# Revit family: 02-60-0035 DN40-500
name_source: partatom
category: Plumbing Fixtures
units: mm (PartAtom-declared; Revit-internal decimal feet)

## family parameters
Always vertical = Yes
Cut with Voids When Loaded = No
Maintain Annotation Orientation = No
Part Type = Normal
Room Calculation Point = No
Round Connector Dimension = Use Diameter
Shared = No
Work Plane-Based = No

## types (21) — shared parameters
1 = 1 mm  [stored 0.00328084 ft]
5 = 5 mm  [stored 0.0164042 ft]
DN040_PN10/16 = 02-040-60-014649
DN050_PN10/16 = 02-050-60-014649
DN065_PN10/16 = 02-065-60-014649
DN080_PN10/16 = 02-080-60-014649
DN100_PN10/16 = 02-100-60-014649
DN125_PN10/16 = 02-125-60-014649
DN150_PN10/16 = 02-150-60-014649
DN200_PN10 = 02-200-60-004649
DN200_PN16 = 02-200-60-014649
DN250_PN10 = 02-250-60-004649
DN250_PN16 = 02-250-60-014649
DN300_PN10 = 02-300-60-004647
DN300_PN16 = 02-300-60-014647
DN350_PN10 = 02-350-60-006
DN350_PN16 = 02-350-60-016
DN400_PN10 = 02-400-60-006
DN400_PN16 = 02-400-60-016
DN450_PN10 = 02-450-60-006
DN450_PN16 = 02-450-60-016
DN500_PN10 = 02-500-60-006
DN500_PN16 = 02-500-60-016
Description_ = AVK GATE VALVE, FLANGED, PN10-16
Search_table = 02-60-0035 DN40-500
URL_product_pages = https://www.avkvalves.com
zero-valued in all types: 50, Default Elevation, Rib4_H, Rib4_L, Rib4_W, Rib5_H, Rib5_L, Rib5_W

## per-type parameters (varying)
- DN040_PN10/16: Body_Arc=125 mm; Body_FL_L=60 mm; Body_FL_R=18 mm  [stored 0.0590551 ft]; Body_FL_T=9 mm  [stored 0.0295276 ft]; Body_FL_W=50 mm; Body_FL_arc=150 mm; Body_FL_rib_dim=164 mm; Body_FL_rib_dim1=105 mm; Body_H=95 mm; Body_L=45 mm; Body_R=8 mm  [stored 0.0262467 ft]; Body_T=10 mm  [stored 0.0328084 ft]; Body_W=43 mm; Body_bottom=15 mm  [stored 0.0492126 ft]; Bonnet_L=41 mm; Bonnet_d1=35 mm  [stored 0.114829 ft]; Bonnet_d2=22 mm  [stored 0.0721785 ft]; Bonnet_dim1=38 mm  [stored 0.124672 ft]; Bonnet_dim2=35 mm  [stored 0.114829 ft]; Bonnet_dim3=23 mm  [stored 0.0754593 ft]; Bore_R=20 mm  [stored 0.0656168 ft]; DN=40 mm; Dh=110 mm; Ds=19 mm  [stored 0.062336 ft]; F=7 mm  [stored 0.0229659 ft]; F1=9 mm  [stored 0.0295276 ft]; F2=29 mm  [stored 0.0951444 ft]; FL_R=70 mm; FL_T=15 mm  [stored 0.0492126 ft]; H=194 mm; H3=269 mm; H3-H=75 mm; L=240 mm; RIB_L=74 mm; RIB_L1=49 mm; RIB_T=6 mm  [stored 0.019685 ft]; Raised_R=45 mm; Raised_dis=3 mm  [stored 0.00984252 ft]; Rib1_H=50 mm; Rib1_L=75 mm; Rib1_R=18 mm  [stored 0.0590551 ft]; Rib1_T=4 mm  [stored 0.0131234 ft]; Rib1_W=45 mm; Rib2_H=50 mm; Rib2_L=70 mm; Rib2_W=45 mm; Rib3_H=50 mm; Rib3_L=50 mm; Rib3_W=45 mm; Rib_T=12 mm  [stored 0.0393701 ft]; Stem=12 mm  [stored 0.0393701 ft]; Sweep _cut=2 mm  [stored 0.00656168 ft]; W=75 mm; Wedge_L=37 mm; logo_H=48 mm; stem1=12 mm  [stored 0.0393701 ft]
- DN050_PN10/16: Body_Arc=150 mm; Body_FL_L=67 mm; Body_FL_R=20 mm  [stored 0.0656168 ft]; Body_FL_T=10 mm  [stored 0.0328084 ft]; Body_FL_W=52 mm; Body_FL_arc=200 mm; Body_FL_rib_dim=179 mm; Body_FL_rib_dim1=106 mm; Body_H=110 mm; Body_L=52 mm; Body_R=10 mm  [stored 0.0328084 ft]; Body_T=10 mm  [stored 0.0328084 ft]; Body_W=45 mm; Body_bottom=22 mm  [stored 0.0721785 ft]; Bonnet_L=47 mm; Bonnet_d1=36 mm  [stored 0.11811 ft]; Bonnet_d2=23 mm  [stored 0.0754593 ft]; Bonnet_dim1=38 mm  [stored 0.124672 ft]; Bonnet_dim2=36 mm  [stored 0.11811 ft]; Bonnet_dim3=23 mm  [stored 0.0754593 ft]; Bore_R=25 mm  [stored 0.082021 ft]; DN=50 mm; Dh=125 mm; Ds=19 mm  [stored 0.062336 ft]; F=7 mm  [stored 0.0229659 ft]; F1=9 mm  [stored 0.0295276 ft]; F2=29 mm  [stored 0.0951444 ft]; FL_R=83 mm; FL_T=19 mm  [stored 0.062336 ft]; H=209 mm; H3=292 mm; H3-H=83 mm; L=250 mm; RIB_L=82 mm; RIB_L1=54 mm; RIB_T=6 mm  [stored 0.019685 ft]; Raised_R=49 mm; Raised_dis=3 mm  [stored 0.00984252 ft]; Rib1_H=60 mm; Rib1_L=80 mm; Rib1_R=20 mm  [stored 0.0656168 ft]; Rib1_T=5 mm  [stored 0.0164042 ft]; Rib1_W=50 mm; Rib2_H=60 mm; Rib2_L=80 mm; Rib2_W=50 mm; Rib3_H=60 mm; Rib3_L=80 mm; Rib3_W=50 mm; Rib_T=16 mm  [stored 0.0524934 ft]; Stem=12 mm  [stored 0.0393701 ft]; Sweep _cut=2 mm  [stored 0.00656168 ft]; W=83 mm; Wedge_L=38 mm  [stored 0.124672 ft]; logo_H=55 mm; stem1=12 mm  [stored 0.0393701 ft]
- DN065_PN10/16: Body_Arc=206 mm; Body_FL_L=86 mm; Body_FL_R=20 mm  [stored 0.0656168 ft]; Body_FL_T=11 mm  [stored 0.0360892 ft]; Body_FL_W=56 mm; Body_FL_arc=775 mm; Body_FL_rib_dim=213 mm; Body_FL_rib_dim1=116 mm; Body_H=102 mm; Body_L=74 mm; Body_R=15 mm  [stored 0.0492126 ft]; Body_T=7 mm  [stored 0.0229659 ft]; Body_W=49 mm; Body_bottom=44 mm; Bonnet_L=67 mm; Bonnet_d1=39 mm; Bonnet_d2=24 mm  [stored 0.0787402 ft]; Bonnet_dim1=48 mm; Bonnet_dim2=39 mm; Bonnet_dim3=29 mm  [stored 0.0951444 ft]; Bore_R=33 mm; DN=65 mm; Dh=154 mm; Ds=19 mm  [stored 0.062336 ft]; F=9 mm  [stored 0.0295276 ft]; F1=12 mm  [stored 0.0393701 ft]; F2=34 mm  [stored 0.111549 ft]; FL_R=97 mm; FL_T=19 mm  [stored 0.062336 ft]; H=243 mm; H3=336 mm; H3-H=93 mm; L=270 mm; RIB_L=94 mm; RIB_L1=62 mm; RIB_T=6 mm  [stored 0.019685 ft]; Raised_R=64 mm; Raised_dis=3 mm  [stored 0.00984252 ft]; Rib1_H=50 mm; Rib1_L=120 mm; Rib1_R=20 mm  [stored 0.0656168 ft]; Rib1_T=5 mm  [stored 0.0164042 ft]; Rib1_W=60 mm; Rib2_H=50 mm; Rib2_L=120 mm; Rib2_W=60 mm; Rib3_H=50 mm; Rib3_L=120 mm; Rib3_W=60 mm; Rib_T=16 mm  [stored 0.0524934 ft]; Stem=14 mm  [stored 0.0459318 ft]; Sweep _cut=2 mm  [stored 0.00656168 ft]; W=95 mm; Wedge_L=41 mm; logo_H=51 mm; stem1=16 mm  [stored 0.0524934 ft]
- DN080_PN10/16: Body_Arc=212 mm; Body_FL_L=86 mm; Body_FL_R=20 mm  [stored 0.0656168 ft]; Body_FL_T=12 mm  [stored 0.0393701 ft]; Body_FL_W=58 mm; Body_FL_arc=775 mm; Body_FL_rib_dim=252 mm; Body_FL_rib_dim1=121 mm; Body_H=108 mm; Body_L=72 mm; Body_R=16 mm  [stored 0.0524934 ft]; Body_T=7 mm  [stored 0.0229659 ft]; Body_W=50 mm; Body_bottom=42 mm; Bonnet_L=65 mm; Bonnet_d1=40 mm; Bonnet_d2=25 mm  [stored 0.082021 ft]; Bonnet_dim1=48 mm; Bonnet_dim2=41 mm; Bonnet_dim3=29 mm  [stored 0.0951444 ft]; Bore_R=40 mm; DN=80 mm; Dh=160 mm; Ds=19 mm  [stored 0.062336 ft]; F=9 mm  [stored 0.0295276 ft]; F1=12 mm  [stored 0.0393701 ft]; F2=34 mm  [stored 0.111549 ft]; FL_R=100 mm; FL_T=19 mm  [stored 0.062336 ft]; H=282 mm; H3=382 mm; H3-H=100 mm; L=280 mm; RIB_L=99 mm; RIB_L1=65 mm; RIB_T=6 mm  [stored 0.019685 ft]; Raised_R=66 mm; Raised_dis=3 mm  [stored 0.00984252 ft]; Rib1_H=58 mm; Rib1_L=120 mm; Rib1_R=20 mm  [stored 0.0656168 ft]; Rib1_T=5 mm  [stored 0.0164042 ft]; Rib1_W=60 mm; Rib2_H=58 mm; Rib2_L=120 mm; Rib2_W=60 mm; Rib3_H=58 mm; Rib3_L=120 mm; Rib3_W=60 mm; Rib_T=16 mm  [stored 0.0524934 ft]; Stem=14 mm  [stored 0.0459318 ft]; Sweep _cut=2 mm  [stored 0.00656168 ft]; W=100 mm; Wedge_L=43 mm; logo_H=54 mm; stem1=16 mm  [stored 0.0524934 ft]
- DN100_PN10/16: Body_Arc=220 mm; Body_FL_L=96 mm; Body_FL_R=20 mm  [stored 0.0656168 ft]; Body_FL_T=13 mm; Body_FL_W=62 mm; Body_FL_arc=400 mm; Body_FL_rib_dim=276 mm; Body_FL_rib_dim1=132 mm; Body_H=122 mm; Body_L=82 mm; Body_R=16 mm  [stored 0.0524934 ft]; Body_T=6 mm  [stored 0.019685 ft]; Body_W=54 mm; Body_bottom=52 mm; Bonnet_L=74 mm; Bonnet_d1=43 mm; Bonnet_d2=27 mm  [stored 0.0885827 ft]; Bonnet_dim1=48 mm; Bonnet_dim2=43 mm; Bonnet_dim3=29 mm  [stored 0.0951444 ft]; Bore_R=50 mm; DN=100 mm; Dh=180 mm; Ds=19 mm  [stored 0.062336 ft]; F=10 mm  [stored 0.0328084 ft]; F1=12 mm  [stored 0.0393701 ft]; F2=34 mm  [stored 0.111549 ft]; FL_R=110 mm; FL_T=18 mm  [stored 0.0590551 ft]; H=306 mm; H3=416 mm; H3-H=110 mm; L=300 mm; RIB_L=117 mm; RIB_L1=76 mm; RIB_T=6 mm  [stored 0.019685 ft]; Raised_R=77 mm; Raised_dis=3 mm  [stored 0.00984252 ft]; Rib1_H=72 mm; Rib1_L=120 mm; Rib1_R=20 mm  [stored 0.0656168 ft]; Rib1_T=5 mm  [stored 0.0164042 ft]; Rib1_W=60 mm; Rib2_H=72 mm; Rib2_L=120 mm; Rib2_W=60 mm; Rib3_H=72 mm; Rib3_L=120 mm; Rib3_W=60 mm; Rib_T=15 mm  [stored 0.0492126 ft]; Stem=14 mm  [stored 0.0459318 ft]; Sweep _cut=2 mm  [stored 0.00656168 ft]; W=118 mm; Wedge_L=46 mm; logo_H=61 mm; stem1=16 mm  [stored 0.0524934 ft]
- DN125_PN10/16: Body_Arc=300 mm; Body_FL_L=110 mm; Body_FL_R=20 mm  [stored 0.0656168 ft]; Body_FL_T=13 mm; Body_FL_W=67 mm; Body_FL_arc=450 mm; Body_FL_rib_dim=316 mm; Body_FL_rib_dim1=145 mm; Body_H=145 mm; Body_L=100 mm; Body_R=16 mm  [stored 0.0524934 ft]; Body_T=6 mm  [stored 0.019685 ft]; Body_W=59 mm; Body_bottom=70 mm; Bonnet_L=90 mm; Bonnet_d1=47 mm; Bonnet_d2=29 mm  [stored 0.0951444 ft]; Bonnet_dim1=48 mm; Bonnet_dim2=47 mm; Bonnet_dim3=29 mm  [stored 0.0951444 ft]; Bore_R=63 mm; DN=125 mm; Dh=190 mm; Ds=20 mm  [stored 0.0656168 ft]; F=10 mm  [stored 0.0328084 ft]; F1=12 mm  [stored 0.0393701 ft]; F2=34 mm  [stored 0.111549 ft]; FL_R=135 mm; FL_T=18 mm  [stored 0.0590551 ft]; H=346 mm; H3=471 mm; H3-H=125 mm; L=325 mm; RIB_L=134 mm; RIB_L1=88 mm; RIB_T=6 mm  [stored 0.019685 ft]; Raised_R=80 mm; Raised_dis=3 mm  [stored 0.00984252 ft]; Rib1_H=90 mm; Rib1_L=120 mm; Rib1_R=20 mm  [stored 0.0656168 ft]; Rib1_T=5 mm  [stored 0.0164042 ft]; Rib1_W=60 mm; Rib2_H=90 mm; Rib2_L=120 mm; Rib2_W=60 mm; Rib3_H=100 mm; Rib3_L=120 mm; Rib3_W=60 mm; Rib_T=15 mm  [stored 0.0492126 ft]; Stem=14 mm  [stored 0.0459318 ft]; Sweep _cut=2 mm  [stored 0.00656168 ft]; W=135 mm; Wedge_L=50 mm; logo_H=73 mm; stem1=16 mm  [stored 0.0524934 ft]
- DN150_PN10/16: Body_Arc=400 mm; Body_FL_L=136 mm; Body_FL_R=20 mm  [stored 0.0656168 ft]; Body_FL_T=13 mm; Body_FL_W=72 mm; Body_FL_arc=300 mm; Body_FL_rib_dim=373 mm; Body_FL_rib_dim1=157 mm; Body_H=172 mm; Body_L=122 mm; Body_R=16 mm  [stored 0.0524934 ft]; Body_T=6 mm  [stored 0.019685 ft]; Body_W=63 mm; Body_bottom=92 mm; Bonnet_L=110 mm; Bonnet_d1=50 mm; Bonnet_d2=32 mm  [stored 0.104987 ft]; Bonnet_dim1=46 mm; Bonnet_dim2=51 mm; Bonnet_dim3=28 mm  [stored 0.0918635 ft]; Bore_R=75 mm; DN=150 mm; Dh=240 mm; Ds=23 mm  [stored 0.0754593 ft]; F=10 mm  [stored 0.0328084 ft]; F1=11 mm  [stored 0.0360892 ft]; F2=34 mm  [stored 0.111549 ft]; FL_R=143 mm; FL_T=18 mm  [stored 0.0590551 ft]; H=403 mm; H3=543 mm; H3-H=140 mm; L=350 mm; RIB_L=149 mm; RIB_L1=98 mm; RIB_T=6 mm  [stored 0.019685 ft]; Raised_R=106 mm; Raised_dis=3 mm  [stored 0.00984252 ft]; Rib1_H=122 mm; Rib1_L=120 mm; Rib1_R=20 mm  [stored 0.0656168 ft]; Rib1_T=5 mm  [stored 0.0164042 ft]; Rib1_W=60 mm; Rib2_H=122 mm; Rib2_L=120 mm; Rib2_W=60 mm; Rib3_H=122 mm; Rib3_L=120 mm; Rib3_W=60 mm; Rib_T=15 mm  [stored 0.0492126 ft]; Stem=14 mm  [stored 0.0459318 ft]; Sweep _cut=2 mm  [stored 0.00656168 ft]; W=150 mm; Wedge_L=54 mm; logo_H=86 mm; stem1=15 mm  [stored 0.0492126 ft]
- DN200_PN10: Body_Arc=500 mm; Body_FL_L=166 mm; Body_FL_R=25 mm  [stored 0.082021 ft]; Body_FL_T=15 mm  [stored 0.0492126 ft]; Body_FL_W=83 mm; Body_FL_arc=450 mm; Body_FL_rib_dim=460 mm; Body_FL_rib_dim1=180 mm; Body_H=220 mm; Body_L=157 mm; Body_R=20 mm  [stored 0.0656168 ft]; Body_T=7 mm  [stored 0.0229659 ft]; Body_W=72 mm; Body_bottom=127 mm; Bonnet_L=141 mm; Bonnet_d1=58 mm; Bonnet_d2=36 mm  [stored 0.11811 ft]; Bonnet_dim1=59 mm; Bonnet_dim2=58 mm; Bonnet_dim3=35 mm  [stored 0.114829 ft]; Bore_R=100 mm; DN=200 mm; Dh=295 mm; Ds=23 mm  [stored 0.0754593 ft]; F=12 mm  [stored 0.0393701 ft]; F1=14 mm  [stored 0.0459318 ft]; F2=34 mm  [stored 0.111549 ft]; FL_R=170 mm; FL_T=20 mm  [stored 0.0656168 ft]; H=490 mm; H3=660 mm; H3-H=170 mm; L=400 mm; RIB_L=187 mm; RIB_L1=122 mm; RIB_T=6 mm  [stored 0.019685 ft]; Raised_R=132 mm; Raised_dis=3 mm  [stored 0.00984252 ft]; Rib1_H=170 mm; Rib1_L=120 mm; Rib1_R=20 mm  [stored 0.0656168 ft]; Rib1_T=5 mm  [stored 0.0164042 ft]; Rib1_W=60 mm; Rib2_H=170 mm; Rib2_L=120 mm; Rib2_W=60 mm; Rib3_H=170 mm; Rib3_L=120 mm; Rib3_W=60 mm; Rib_T=17 mm  [stored 0.0557743 ft]; Stem=14 mm  [stored 0.0459318 ft]; Sweep _cut=3 mm  [stored 0.00984252 ft]; W=188 mm; Wedge_L=61 mm; logo_H=110 mm; stem1=19 mm  [stored 0.062336 ft]
- DN200_PN16: Body_Arc=500 mm; Body_FL_L=166 mm; Body_FL_R=25 mm  [stored 0.082021 ft]; Body_FL_T=15 mm  [stored 0.0492126 ft]; Body_FL_W=83 mm; Body_FL_arc=450 mm; Body_FL_rib_dim=460 mm; Body_FL_rib_dim1=180 mm; Body_H=220 mm; Body_L=157 mm; Body_R=20 mm  [stored 0.0656168 ft]; Body_T=7 mm  [stored 0.0229659 ft]; Body_W=72 mm; Body_bottom=127 mm; Bonnet_L=141 mm; Bonnet_d1=58 mm; Bonnet_d2=36 mm  [stored 0.11811 ft]; Bonnet_dim1=59 mm; Bonnet_dim2=58 mm; Bonnet_dim3=35 mm  [stored 0.114829 ft]; Bore_R=100 mm; DN=200 mm; Dh=295 mm; Ds=23 mm  [stored 0.0754593 ft]; F=12 mm  [stored 0.0393701 ft]; F1=14 mm  [stored 0.0459318 ft]; F2=34 mm  [stored 0.111549 ft]; FL_R=170 mm; FL_T=20 mm  [stored 0.0656168 ft]; H=490 mm; H3=660 mm; H3-H=170 mm; L=400 mm; RIB_L=187 mm; RIB_L1=122 mm; RIB_T=6 mm  [stored 0.019685 ft]; Raised_R=132 mm; Raised_dis=3 mm  [stored 0.00984252 ft]; Rib1_H=170 mm; Rib1_L=120 mm; Rib1_R=20 mm  [stored 0.0656168 ft]; Rib1_T=5 mm  [stored 0.0164042 ft]; Rib1_W=60 mm; Rib2_H=170 mm; Rib2_L=120 mm; Rib2_W=60 mm; Rib3_H=170 mm; Rib3_L=120 mm; Rib3_W=60 mm; Rib_T=17 mm  [stored 0.0557743 ft]; Stem=14 mm  [stored 0.0459318 ft]; Sweep _cut=3 mm  [stored 0.00984252 ft]; W=188 mm; Wedge_L=61 mm; logo_H=110 mm; stem1=19 mm  [stored 0.062336 ft]
- DN300_PN10: Body_Arc=900 mm; Body_FL_L=228 mm; Body_FL_R=30 mm  [stored 0.0984252 ft]; Body_FL_T=23 mm  [stored 0.0754593 ft]; Body_FL_W=104 mm; Body_FL_arc=1000 mm; Body_FL_rib_dim=676 mm; Body_FL_rib_dim1=230 mm; Body_H=370 mm; Body_L=205 mm; Body_R=30 mm  [stored 0.0984252 ft]; Body_T=9 mm  [stored 0.0295276 ft]; Body_W=90 mm; Body_bottom=175 mm; Bonnet_L=185 mm; Bonnet_d1=72 mm; Bonnet_d2=45 mm; Bonnet_dim1=76 mm; Bonnet_dim2=72 mm; Bonnet_dim3=45 mm; Bore_R=150 mm; DN=300 mm; Dh=400 mm; Ds=23 mm  [stored 0.0754593 ft]; F=14 mm  [stored 0.0459318 ft]; F1=18 mm  [stored 0.0590551 ft]; F2=47 mm; FL_R=228 mm; FL_T=20 mm  [stored 0.0656168 ft]; H=706 mm; H3=934 mm; H3-H=228 mm; L=500 mm; RIB_L=227 mm; RIB_L1=148 mm; RIB_T=4 mm  [stored 0.0131234 ft]; Raised_R=184 mm; Raised_dis=2 mm  [stored 0.00656168 ft]; Rib1_H=245 mm; Rib1_L=432 mm; Rib1_R=65 mm; Rib1_T=8 mm  [stored 0.0262467 ft]; Rib1_W=220 mm; Rib2_H=170 mm; Rib2_L=432 mm; Rib2_W=220 mm; Rib3_H=190 mm; Rib3_L=280 mm; Rib3_W=150 mm; Rib_T=18 mm  [stored 0.0590551 ft]; Stem=19 mm  [stored 0.062336 ft]; Sweep _cut=4 mm  [stored 0.0131234 ft]; W=228 mm; Wedge_L=77 mm; logo_H=185 mm; stem1=24 mm  [stored 0.0787402 ft]
- DN300_PN16: Body_Arc=900 mm; Body_FL_L=228 mm; Body_FL_R=30 mm  [stored 0.0984252 ft]; Body_FL_T=23 mm  [stored 0.0754593 ft]; Body_FL_W=104 mm; Body_FL_arc=1000 mm; Body_FL_rib_dim=676 mm; Body_FL_rib_dim1=230 mm; Body_H=370 mm; Body_L=205 mm; Body_R=30 mm  [stored 0.0984252 ft]; Body_T=9 mm  [stored 0.0295276 ft]; Body_W=90 mm; Body_bottom=175 mm; Bonnet_L=185 mm; Bonnet_d1=72 mm; Bonnet_d2=45 mm; Bonnet_dim1=76 mm; Bonnet_dim2=72 mm; Bonnet_dim3=45 mm; Bore_R=150 mm; DN=300 mm; Dh=410 mm; Ds=28 mm  [stored 0.0918635 ft]; F=14 mm  [stored 0.0459318 ft]; F1=18 mm  [stored 0.0590551 ft]; F2=47 mm; FL_R=228 mm; FL_T=20 mm  [stored 0.0656168 ft]; H=706 mm; H3=934 mm; H3-H=228 mm; L=500 mm; RIB_L=227 mm; RIB_L1=148 mm; RIB_T=4 mm  [stored 0.0131234 ft]; Raised_R=184 mm; Raised_dis=2 mm  [stored 0.00656168 ft]; Rib1_H=245 mm; Rib1_L=432 mm; Rib1_R=65 mm; Rib1_T=8 mm  [stored 0.0262467 ft]; Rib1_W=220 mm; Rib2_H=170 mm; Rib2_L=432 mm; Rib2_W=220 mm; Rib3_H=190 mm; Rib3_L=280 mm; Rib3_W=150 mm; Rib_T=18 mm  [stored 0.0590551 ft]; Stem=19 mm  [stored 0.062336 ft]; Sweep _cut=4 mm  [stored 0.0131234 ft]; W=228 mm; Wedge_L=77 mm; logo_H=185 mm; stem1=24 mm  [stored 0.0787402 ft]
- DN350_PN10: Body_Arc=1120 mm; Body_FL_L=282 mm; Body_FL_R=40 mm; Body_FL_T=28 mm  [stored 0.0918635 ft]; Body_FL_W=114 mm; Body_FL_arc=1550 mm; Body_FL_rib_dim=917 mm; Body_FL_rib_dim1=251 mm; Body_H=485 mm; Body_L=238 mm; Body_R=30 mm  [stored 0.0984252 ft]; Body_T=13 mm; Body_W=99 mm; Body_bottom=208 mm; Bonnet_L=214 mm; Bonnet_d1=79 mm; Bonnet_d2=50 mm; Bonnet_dim1=84 mm; Bonnet_dim2=80 mm; Bonnet_dim3=50 mm; Bore_R=175 mm; DN=350 mm; Dh=460 mm; Ds=23 mm  [stored 0.0754593 ft]; F=16 mm  [stored 0.0524934 ft]; F1=20 mm  [stored 0.0656168 ft]; F2=55 mm; FL_R=520 mm; FL_T=25 mm  [stored 0.082021 ft]; H=947 mm; H3=1207 mm; H3-H=260 mm; L=550 mm; RIB_L=281 mm; RIB_L1=183 mm; RIB_T=8 mm  [stored 0.0262467 ft]; Raised_R=215 mm; Raised_dis=4 mm  [stored 0.0131234 ft]; Rib1_H=410 mm; Rib1_L=560 mm; Rib1_R=65 mm; Rib1_T=9 mm  [stored 0.0295276 ft]; Rib1_W=306 mm; Rib2_H=290 mm; Rib2_L=560 mm; Rib2_W=306 mm; Rib3_H=170 mm; Rib3_L=560 mm; Rib3_W=306 mm; Rib_T=21 mm; Stem=22 mm  [stored 0.0721785 ft]; Sweep _cut=5 mm  [stored 0.0164042 ft]; W=282 mm; Wedge_L=84 mm; logo_H=243 mm; stem1=27 mm  [stored 0.0885827 ft]
- DN350_PN16: Body_Arc=1120 mm; Body_FL_L=282 mm; Body_FL_R=40 mm; Body_FL_T=28 mm  [stored 0.0918635 ft]; Body_FL_W=114 mm; Body_FL_arc=1550 mm; Body_FL_rib_dim=917 mm; Body_FL_rib_dim1=251 mm; Body_H=485 mm; Body_L=238 mm; Body_R=30 mm  [stored 0.0984252 ft]; Body_T=13 mm; Body_W=99 mm; Body_bottom=208 mm; Bonnet_L=214 mm; Bonnet_d1=79 mm; Bonnet_d2=50 mm; Bonnet_dim1=84 mm; Bonnet_dim2=80 mm; Bonnet_dim3=50 mm; Bore_R=175 mm; DN=350 mm; Dh=470 mm; Ds=28 mm  [stored 0.0918635 ft]; F=16 mm  [stored 0.0524934 ft]; F1=20 mm  [stored 0.0656168 ft]; F2=55 mm; FL_R=520 mm; FL_T=25 mm  [stored 0.082021 ft]; H=947 mm; H3=1207 mm; H3-H=260 mm; L=550 mm; RIB_L=281 mm; RIB_L1=183 mm; RIB_T=8 mm  [stored 0.0262467 ft]; Raised_R=215 mm; Raised_dis=4 mm  [stored 0.0131234 ft]; Rib1_H=410 mm; Rib1_L=560 mm; Rib1_R=65 mm; Rib1_T=9 mm  [stored 0.0295276 ft]; Rib1_W=306 mm; Rib2_H=290 mm; Rib2_L=560 mm; Rib2_W=306 mm; Rib3_H=170 mm; Rib3_L=560 mm; Rib3_W=306 mm; Rib_T=21 mm; Stem=22 mm  [stored 0.0721785 ft]; Sweep _cut=5 mm  [stored 0.0164042 ft]; W=282 mm; Wedge_L=84 mm; logo_H=243 mm; stem1=27 mm  [stored 0.0885827 ft]
- DN400_PN10: Body_Arc=1120 mm; Body_FL_L=290 mm; Body_FL_R=50 mm; Body_FL_T=30 mm  [stored 0.0984252 ft]; Body_FL_W=124 mm; Body_FL_arc=1159 mm; Body_FL_rib_dim=929 mm; Body_FL_rib_dim1=276 mm; Body_H=512 mm; Body_L=238 mm; Body_R=30 mm  [stored 0.0984252 ft]; Body_T=13 mm; Body_W=108 mm; Body_bottom=208 mm; Bonnet_L=214 mm; Bonnet_d1=86 mm; Bonnet_d2=54 mm; Bonnet_dim1=84 mm; Bonnet_dim2=87 mm; Bonnet_dim3=50 mm; Bore_R=200 mm; DN=400 mm; Dh=515 mm; Ds=28 mm  [stored 0.0918635 ft]; F=16 mm  [stored 0.0524934 ft]; F1=20 mm  [stored 0.0656168 ft]; F2=55 mm; FL_R=290 mm; FL_T=25 mm  [stored 0.082021 ft]; H=959 mm; H3=1249 mm; H3-H=290 mm; L=600 mm; RIB_L=289 mm; RIB_L1=189 mm; RIB_T=8 mm  [stored 0.0262467 ft]; Raised_R=241 mm; Raised_dis=4 mm  [stored 0.0131234 ft]; Rib1_H=430 mm; Rib1_L=538 mm; Rib1_R=70 mm; Rib1_T=10 mm  [stored 0.0328084 ft]; Rib1_W=326 mm; Rib2_H=320 mm; Rib2_L=538 mm; Rib2_W=326 mm; Rib3_H=173 mm; Rib3_L=538 mm; Rib3_W=326 mm; Rib_T=21 mm; Stem=22 mm  [stored 0.0721785 ft]; Sweep _cut=5 mm  [stored 0.0164042 ft]; W=290 mm; Wedge_L=92 mm; logo_H=256 mm; stem1=27 mm  [stored 0.0885827 ft]
- DN400_PN16: Body_Arc=1120 mm; Body_FL_L=290 mm; Body_FL_R=50 mm; Body_FL_T=30 mm  [stored 0.0984252 ft]; Body_FL_W=124 mm; Body_FL_arc=1159 mm; Body_FL_rib_dim=929 mm; Body_FL_rib_dim1=276 mm; Body_H=512 mm; Body_L=238 mm; Body_R=30 mm  [stored 0.0984252 ft]; Body_T=13 mm; Body_W=108 mm; Body_bottom=208 mm; Bonnet_L=214 mm; Bonnet_d1=86 mm; Bonnet_d2=54 mm; Bonnet_dim1=84 mm; Bonnet_dim2=87 mm; Bonnet_dim3=50 mm; Bore_R=200 mm; DN=400 mm; Dh=525 mm; Ds=31 mm  [stored 0.101706 ft]; F=16 mm  [stored 0.0524934 ft]; F1=20 mm  [stored 0.0656168 ft]; F2=55 mm; FL_R=290 mm; FL_T=25 mm  [stored 0.082021 ft]; H=959 mm; H3=1249 mm; H3-H=290 mm; L=600 mm; RIB_L=289 mm; RIB_L1=189 mm; RIB_T=8 mm  [stored 0.0262467 ft]; Raised_R=241 mm; Raised_dis=4 mm  [stored 0.0131234 ft]; Rib1_H=430 mm; Rib1_L=538 mm; Rib1_R=70 mm; Rib1_T=10 mm  [stored 0.0328084 ft]; Rib1_W=326 mm; Rib2_H=320 mm; Rib2_L=538 mm; Rib2_W=326 mm; Rib3_H=173 mm; Rib3_L=538 mm; Rib3_W=326 mm; Rib_T=21 mm; Stem=22 mm  [stored 0.0721785 ft]; Sweep _cut=5 mm  [stored 0.0164042 ft]; W=290 mm; Wedge_L=92 mm; logo_H=256 mm; stem1=27 mm  [stored 0.0885827 ft]
- DN450_PN10: Body_Arc=1200 mm; Body_FL_L=325 mm; Body_FL_R=55 mm; Body_FL_T=30 mm  [stored 0.0984252 ft]; Body_FL_W=135 mm; Body_FL_arc=1300 mm; Body_FL_rib_dim=928 mm; Body_FL_rib_dim1=295 mm; Body_H=500 mm; Body_L=300 mm; Body_R=35 mm  [stored 0.114829 ft]; Body_T=14 mm  [stored 0.0459318 ft]; Body_W=117 mm; Body_bottom=270 mm; Bonnet_L=270 mm; Bonnet_d1=94 mm; Bonnet_d2=59 mm; Bonnet_dim1=84 mm; Bonnet_dim2=94 mm; Bonnet_dim3=50 mm; Bore_R=225 mm; DN=450 mm; Dh=585 mm; Ds=31 mm  [stored 0.101706 ft]; F=16 mm  [stored 0.0524934 ft]; F1=20 mm  [stored 0.0656168 ft]; F2=55 mm; FL_R=320 mm; FL_T=30 mm  [stored 0.0984252 ft]; H=958 mm; H3=1278 mm; H3-H=320 mm; L=650 mm; RIB_L=319 mm; RIB_L1=208 mm; RIB_T=8 mm  [stored 0.0262467 ft]; Raised_R=260 mm; Raised_dis=4 mm  [stored 0.0131234 ft]; Rib1_H=415 mm; Rib1_L=827 mm; Rib1_R=75 mm; Rib1_T=11 mm  [stored 0.0360892 ft]; Rib1_W=350 mm; Rib2_H=290 mm; Rib2_L=827 mm; Rib2_W=350 mm; Rib3_H=180 mm; Rib3_L=827 mm; Rib3_W=350 mm; Rib_T=26 mm; Stem=22 mm  [stored 0.0721785 ft]; Sweep _cut=5 mm  [stored 0.0164042 ft]; W=320 mm; Wedge_L=99 mm; logo_H=250 mm; stem1=27 mm  [stored 0.0885827 ft]
- DN450_PN16: Body_Arc=1200 mm; Body_FL_L=325 mm; Body_FL_R=55 mm; Body_FL_T=30 mm  [stored 0.0984252 ft]; Body_FL_W=135 mm; Body_FL_arc=1300 mm; Body_FL_rib_dim=928 mm; Body_FL_rib_dim1=295 mm; Body_H=500 mm; Body_L=300 mm; Body_R=35 mm  [stored 0.114829 ft]; Body_T=14 mm  [stored 0.0459318 ft]; Body_W=117 mm; Body_bottom=270 mm; Bonnet_L=270 mm; Bonnet_d1=94 mm; Bonnet_d2=59 mm; Bonnet_dim1=84 mm; Bonnet_dim2=94 mm; Bonnet_dim3=50 mm; Bore_R=225 mm; DN=450 mm; Dh=585 mm; Ds=31 mm  [stored 0.101706 ft]; F=16 mm  [stored 0.0524934 ft]; F1=20 mm  [stored 0.0656168 ft]; F2=55 mm; FL_R=320 mm; FL_T=30 mm  [stored 0.0984252 ft]; H=958 mm; H3=1278 mm; H3-H=320 mm; L=650 mm; RIB_L=319 mm; RIB_L1=208 mm; RIB_T=8 mm  [stored 0.0262467 ft]; Raised_R=260 mm; Raised_dis=4 mm  [stored 0.0131234 ft]; Rib1_H=415 mm; Rib1_L=827 mm; Rib1_R=75 mm; Rib1_T=11 mm  [stored 0.0360892 ft]; Rib1_W=350 mm; Rib2_H=290 mm; Rib2_L=827 mm; Rib2_W=350 mm; Rib3_H=180 mm; Rib3_L=827 mm; Rib3_W=350 mm; Rib_T=26 mm; Stem=22 mm  [stored 0.0721785 ft]; Sweep _cut=5 mm  [stored 0.0164042 ft]; W=320 mm; Wedge_L=99 mm; logo_H=250 mm; stem1=27 mm  [stored 0.0885827 ft]
- DN500_PN10: Body_Arc=1200 mm; Body_FL_L=360 mm; Body_FL_R=60 mm; Body_FL_T=33 mm; Body_FL_W=145 mm; Body_FL_arc=1350 mm; Body_FL_rib_dim=928 mm; Body_FL_rib_dim1=319 mm; Body_H=500 mm; Body_L=353 mm; Body_R=50 mm; Body_T=14 mm  [stored 0.0459318 ft]; Body_W=126 mm; Body_bottom=323 mm; Bonnet_L=318 mm; Bonnet_d1=101 mm; Bonnet_d2=63 mm; Bonnet_dim1=84 mm; Bonnet_dim2=101 mm; Bonnet_dim3=50 mm; Bore_R=250 mm; DN=500 mm; Dh=650 mm; Ds=34 mm  [stored 0.111549 ft]; F=16 mm  [stored 0.0524934 ft]; F1=20 mm  [stored 0.0656168 ft]; F2=55 mm; FL_R=353 mm; FL_T=32 mm  [stored 0.104987 ft]; H=958 mm; H3=1316 mm; H3-H=358 mm; L=700 mm; RIB_L=357 mm; RIB_L1=232 mm; RIB_T=8 mm  [stored 0.0262467 ft]; Raised_R=290 mm; Raised_dis=4 mm  [stored 0.0131234 ft]; Rib1_H=400 mm; Rib1_L=840 mm; Rib1_R=75 mm; Rib1_T=11 mm  [stored 0.0360892 ft]; Rib1_W=370 mm; Rib2_H=315 mm; Rib2_L=840 mm; Rib2_W=370 mm; Rib3_H=190 mm; Rib3_L=840 mm; Rib3_W=370 mm; Rib_T=28 mm  [stored 0.0918635 ft]; Stem=22 mm  [stored 0.0721785 ft]; Sweep _cut=5 mm  [stored 0.0164042 ft]; W=358 mm; Wedge_L=107 mm; logo_H=250 mm; stem1=27 mm  [stored 0.0885827 ft]
- DN500_PN16: Body_Arc=1200 mm; Body_FL_L=360 mm; Body_FL_R=60 mm; Body_FL_T=33 mm; Body_FL_W=145 mm; Body_FL_arc=1350 mm; Body_FL_rib_dim=928 mm; Body_FL_rib_dim1=319 mm; Body_H=500 mm; Body_L=353 mm; Body_R=50 mm; Body_T=14 mm  [stored 0.0459318 ft]; Body_W=126 mm; Body_bottom=323 mm; Bonnet_L=318 mm; Bonnet_d1=101 mm; Bonnet_d2=63 mm; Bonnet_dim1=84 mm; Bonnet_dim2=101 mm; Bonnet_dim3=50 mm; Bore_R=250 mm; DN=500 mm; Dh=650 mm; Ds=34 mm  [stored 0.111549 ft]; F=16 mm  [stored 0.0524934 ft]; F1=20 mm  [stored 0.0656168 ft]; F2=55 mm; FL_R=353 mm; FL_T=32 mm  [stored 0.104987 ft]; H=958 mm; H3=1316 mm; H3-H=358 mm; L=700 mm; RIB_L=357 mm; RIB_L1=232 mm; RIB_T=8 mm  [stored 0.0262467 ft]; Raised_R=290 mm; Raised_dis=4 mm  [stored 0.0131234 ft]; Rib1_H=400 mm; Rib1_L=840 mm; Rib1_R=75 mm; Rib1_T=11 mm  [stored 0.0360892 ft]; Rib1_W=370 mm; Rib2_H=315 mm; Rib2_L=840 mm; Rib2_W=370 mm; Rib3_H=190 mm; Rib3_L=840 mm; Rib3_W=370 mm; Rib_T=28 mm  [stored 0.0918635 ft]; Stem=22 mm  [stored 0.0721785 ft]; Sweep _cut=5 mm  [stored 0.0164042 ft]; W=358 mm; Wedge_L=107 mm; logo_H=250 mm; stem1=27 mm  [stored 0.0885827 ft]
- DN250_PN10: Body_Arc=900 mm; Body_FL_L=211 mm; Body_FL_R=25 mm  [stored 0.082021 ft]; Body_FL_T=15 mm  [stored 0.0492126 ft]; Body_FL_W=93 mm; Body_FL_arc=1000 mm; Body_FL_rib_dim=595 mm; Body_FL_rib_dim1=205 mm; Body_H=285 mm; Body_L=196 mm; Body_R=25 mm  [stored 0.082021 ft]; Body_T=9 mm  [stored 0.0295276 ft]; Body_W=81 mm; Body_bottom=166 mm; Bonnet_L=176 mm; Bonnet_d1=65 mm; Bonnet_d2=41 mm; Bonnet_dim1=76 mm; Bonnet_dim2=65 mm; Bonnet_dim3=45 mm; Bore_R=125 mm; DN=250 mm; Dh=350 mm; Ds=23 mm  [stored 0.0754593 ft]; F=14 mm  [stored 0.0459318 ft]; F1=18 mm  [stored 0.0590551 ft]; F2=47 mm; FL_R=200 mm; FL_T=20 mm  [stored 0.0656168 ft]; H=625 mm; H3=825 mm; H3-H=200 mm; L=450 mm; RIB_L=199 mm; RIB_L1=130 mm; RIB_T=4 mm  [stored 0.0131234 ft]; Raised_R=160 mm; Raised_dis=2 mm  [stored 0.00656168 ft]; Rib1_H=200 mm; Rib1_L=420 mm; Rib1_R=60 mm; Rib1_T=8 mm  [stored 0.0262467 ft]; Rib1_W=195 mm; Rib2_H=160 mm; Rib2_L=200 mm; Rib2_W=140 mm; Rib3_H=220 mm; Rib3_L=200 mm; Rib3_W=140 mm; Rib_T=18 mm  [stored 0.0590551 ft]; Stem=19 mm  [stored 0.062336 ft]; Sweep _cut=3 mm  [stored 0.00984252 ft]; W=200 mm; Wedge_L=69 mm; logo_H=143 mm; stem1=24 mm  [stored 0.0787402 ft]
- DN250_PN16: Body_Arc=900 mm; Body_FL_L=211 mm; Body_FL_R=25 mm  [stored 0.082021 ft]; Body_FL_T=15 mm  [stored 0.0492126 ft]; Body_FL_W=93 mm; Body_FL_arc=1000 mm; Body_FL_rib_dim=595 mm; Body_FL_rib_dim1=205 mm; Body_H=285 mm; Body_L=196 mm; Body_R=25 mm  [stored 0.082021 ft]; Body_T=9 mm  [stored 0.0295276 ft]; Body_W=81 mm; Body_bottom=166 mm; Bonnet_L=176 mm; Bonnet_d1=65 mm; Bonnet_d2=41 mm; Bonnet_dim1=76 mm; Bonnet_dim2=65 mm; Bonnet_dim3=45 mm; Bore_R=125 mm; DN=250 mm; Dh=355 mm; Ds=28 mm  [stored 0.0918635 ft]; F=14 mm  [stored 0.0459318 ft]; F1=18 mm  [stored 0.0590551 ft]; F2=47 mm; FL_R=200 mm; FL_T=20 mm  [stored 0.0656168 ft]; H=625 mm; H3=825 mm; H3-H=200 mm; L=450 mm; RIB_L=199 mm; RIB_L1=130 mm; RIB_T=4 mm  [stored 0.0131234 ft]; Raised_R=160 mm; Raised_dis=2 mm  [stored 0.00656168 ft]; Rib1_H=200 mm; Rib1_L=420 mm; Rib1_R=60 mm; Rib1_T=8 mm  [stored 0.0262467 ft]; Rib1_W=195 mm; Rib2_H=160 mm; Rib2_L=200 mm; Rib2_W=140 mm; Rib3_H=220 mm; Rib3_L=200 mm; Rib3_W=140 mm; Rib_T=18 mm  [stored 0.0590551 ft]; Stem=19 mm  [stored 0.062336 ft]; Sweep _cut=3 mm  [stored 0.00984252 ft]; W=200 mm; Wedge_L=69 mm; logo_H=143 mm; stem1=24 mm  [stored 0.0787402 ft]

note: [stored X ft] marks values corroborated as IEEE doubles in the binary element streams (Revit-internal decimal feet)

## geometry (parser evidence)
native form markers: Sweep x5
no freeform markers — native parametric forms only
